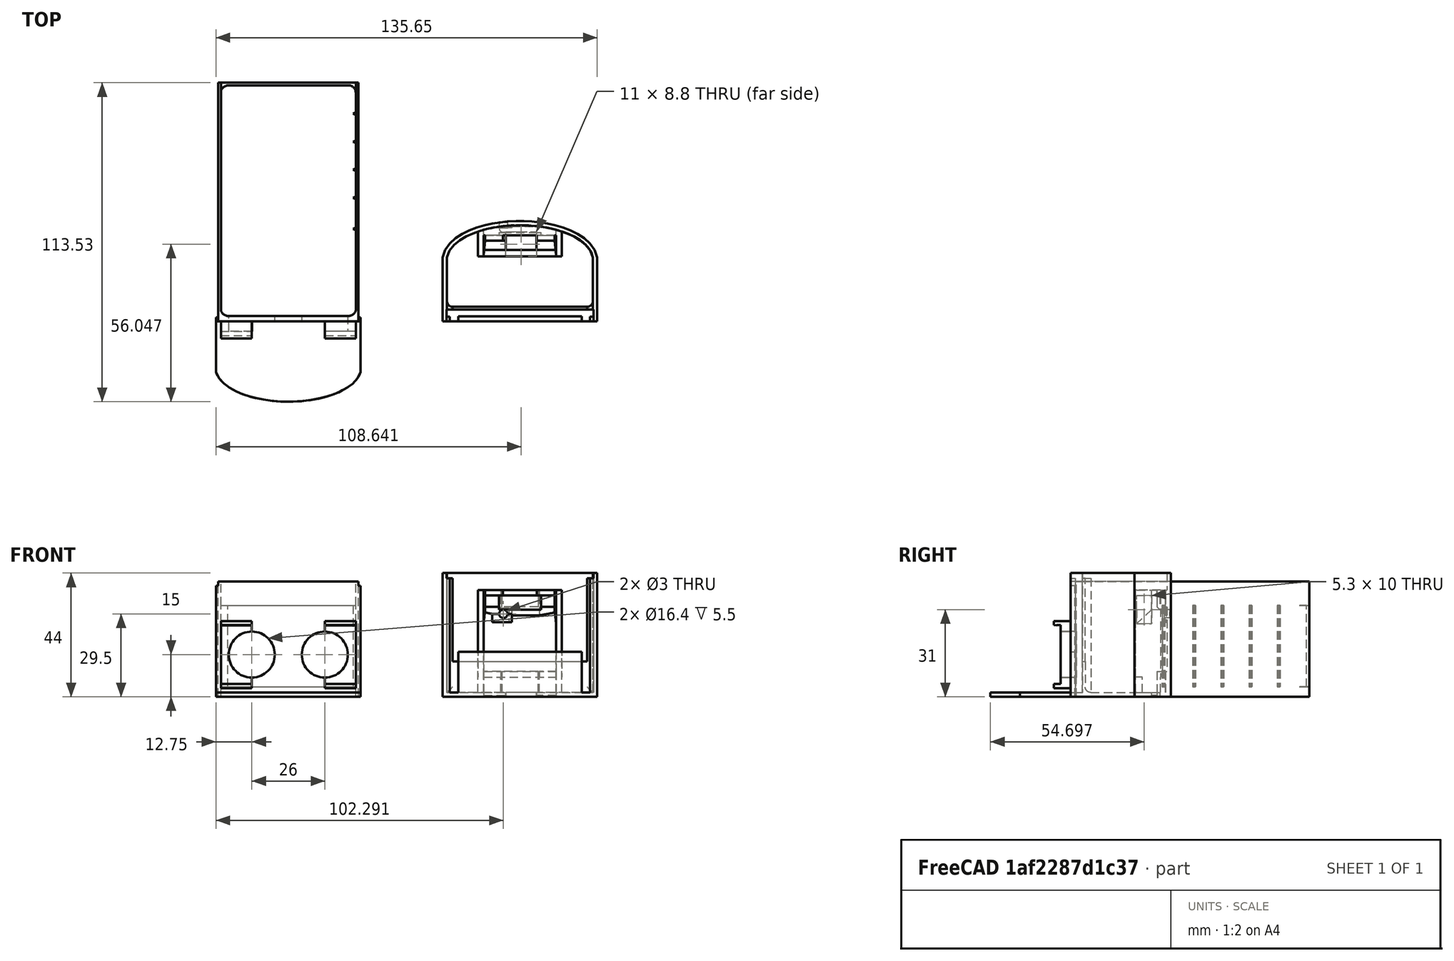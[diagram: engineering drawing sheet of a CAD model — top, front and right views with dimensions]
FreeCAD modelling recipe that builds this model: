
FCSTD DOCUMENT  (FreeCAD 0.18.4R)
Label: sonic.sensor.V6
License: All rights reserved
LicenseURL: http://en.wikipedia.org/wiki/All_rights_reserved
objects: Part::Feature×10, Part::Extrusion×10, Part::Cut×9, Part::Part2DObjectPython×5, Part::MultiFuse×2
note: 36 computed .brp shape members not serialized (recipe doc carries the construction recipe); baked Part::Feature solids carry a one-line shape summary decoded from their .brp

FEATURE [Part::Feature] Fusion025001001  label="Fusion025007"
  shape: bbox 51.5 x 91 x 41 mm, 79 faces (baked)
FEATURE [Part::Feature] Cut047001  label="Cut048"
  shape: bbox 54.92 x 35.75 x 44 mm, 100 faces (baked)
FEATURE [Part::Feature] Cut  label="Cut047008"
  Placement = pos=(-82.4397,-54.2833,45.5) rot=(1,0,0;3.14159rad)
  shape: bbox 51.9 x 28.53 x 1.5 mm, 8 faces (baked)
FEATURE [Part::Feature] Face001
  Placement = pos=(-82.4397,-54.2833,45.5) rot=(1,0,0;3.14159rad)
  shape: bbox 1.021e-05 x 15.53 x 1.5 mm, 1 faces, 0 solids (baked)
FEATURE [Part::Extrusion] Extrusion
  Base = -> Face001
  Dir = (-0.202449,-2e-16,0)
  DirMode = 0
  FaceMakerClass = Part::FaceMakerBullseye
  LengthFwd = 0
  LengthRev = 0
  Solid = true
  Symmetric = false
FEATURE [Part::Feature] Face002
  Placement = pos=(-82.4397,-54.2833,45.5) rot=(1,0,0;3.14159rad)
  shape: bbox 1.02e-05 x 1.5 x 1.5 mm, 1 faces, 0 solids (baked)
FEATURE [Part::Extrusion] Extrusion001
  Base = -> Face002
  Dir = (-0.2,0,0)
  DirMode = 0
  FaceMakerClass = Part::FaceMakerBullseye
  LengthFwd = 0
  LengthRev = 0
  Solid = true
  Symmetric = false
FEATURE [Part::Cut] Cut047002
  Base = -> Cut
  Tool = -> Extrusion001
FEATURE [Part::Cut] Cut047003
  Base = -> Cut047002
  Tool = -> Extrusion
FEATURE [Part::Feature] Face
  Placement = pos=(-82.4397,-54.2833,45.5) rot=(1,0,0;3.14159rad)
  shape: bbox 1.022e-05 x 17.03 x 1.5 mm, 1 faces, 0 solids (baked)
FEATURE [Part::Extrusion] Extrusion002
  Base = -> Face
  Dir = (0.2,3.56116e-11,0)
  DirMode = 0
  FaceMakerClass = Part::FaceMakerBullseye
  LengthFwd = 0
  LengthRev = 0
  Solid = true
  Symmetric = false
FEATURE [Part::Cut] Cut047004
  Base = -> Cut047003
  Tool = -> Extrusion002
FEATURE [Part::Part2DObjectPython] Rectangle  # Draft 2D object (typed FeaturePython)
  ChamferSize = 0
  Columns = 1
  FilletRadius = 0
  Height = 6.48539
  Length = 13.196
  MakeFace = true
  Placement = pos=(50.75,-56.2171,-3.37764) rot=(0.57735,0.57735,0.57735;2.0944rad)
  Rows = 1
  Support = -> [Cut047004]
FEATURE [Part::Extrusion] Extrusion003
  Base = -> Rectangle
  Dir = (5.57169,3.7e-15,-3.1e-15)
  DirMode = 0
  FaceMakerClass = Part::FaceMakerBullseye
  LengthFwd = 0
  LengthRev = 0
  Solid = true
  Symmetric = false
FEATURE [Part::Cut] Cut047005
  Base = -> Cut047004
  Tool = -> Extrusion003
FEATURE [Part::Part2DObjectPython] Rectangle001  # Draft 2D object (typed FeaturePython)
  ChamferSize = 0
  Columns = 1
  FilletRadius = 0
  Height = 9.74903
  Length = 15.1226
  MakeFace = true
  Placement = pos=(-0.75,-44.1427,-2.99245) rot=(0.57735,-0.57735,-0.57735;2.0944rad)
  Rows = 1
  Support = -> [Cut047005]
FEATURE [Part::Extrusion] Extrusion004
  Base = -> Rectangle001
  Dir = (-5.48636,-1.54403e-09,1.54403e-09)
  DirMode = 0
  FaceMakerClass = Part::FaceMakerBullseye
  LengthFwd = 0
  LengthRev = 0
  Solid = true
  Symmetric = false
FEATURE [Part::Cut] Cut047006
  Base = -> Cut047005
  Tool = -> Extrusion004
FEATURE [Part::MultiFuse] Fusion
  Shapes = -> [Cut047006,Fusion025001001]
FEATURE [Part::Part2DObjectPython] Rectangle002  # Draft 2D object (typed FeaturePython)
  ChamferSize = 0
  Columns = 1
  FilletRadius = 0
  Height = 15.8443
  Length = 3.14753
  MakeFace = true
  Placement = pos=(130.245,-38.6276,44) rot=(0,0,1;0rad)
  Rows = 1
FEATURE [Part::Part2DObjectPython] Rectangle004  # Draft 2D object (typed FeaturePython)
  ChamferSize = 0
  Columns = 1
  FilletRadius = 0
  Height = 15.3179
  Length = 4.9835
  MakeFace = true
  Placement = pos=(81.4897,-38.1013,44) rot=(0,0,1;0rad)
  Rows = 1
FEATURE [Part::Part2DObjectPython] Line001  # Draft 2D object (typed FeaturePython)
  ChamferSize = 0
  Closed = false
  End = (-0.75,-37.0713,5.991e-13)
  FilletRadius = 0
  Length = 1.5
  MakeFace = true
  Placement = pos=(-0.75,-37.0713,1.5) rot=(0.57735,-0.57735,-0.57735;2.0944rad)
  Points = (2) [(0,0,0),(-1.25084e-10,-1.5,-2.62753e-09)]
  Start = (-0.75,-37.0713,1.5)
  Subdivisions = 0
  Support = -> [Fusion]
FEATURE [Part::Extrusion] Extrusion005
  Base = -> Rectangle004
  Dir = (-1e-16,4e-16,-1.8)
  DirMode = 0
  FaceMakerClass = Part::FaceMakerBullseye
  LengthFwd = 0
  LengthRev = 0
  Solid = true
  Symmetric = false
FEATURE [Part::Extrusion] Extrusion006
  Base = -> Rectangle002
  Dir = (-1e-16,4e-16,-1.8)
  DirMode = 0
  FaceMakerClass = Part::FaceMakerBullseye
  LengthFwd = 0
  LengthRev = 0
  Solid = true
  Symmetric = false
FEATURE [Part::Cut] Cut047007
  Base = -> Cut047001
  Tool = -> Extrusion006
FEATURE [Part::Cut] Cut047008  label="Cut047009"
  Base = -> Cut047007
  Tool = -> Extrusion005
FEATURE [Part::Feature] Face003
  shape: bbox 1.02e-05 x 1.717 x 1.8 mm, 1 faces, 0 solids (baked)
FEATURE [Part::Extrusion] Extrusion007
  Base = -> Face003
  Dir = (-0.2,0,0)
  DirMode = 0
  FaceMakerClass = Part::FaceMakerBullseye
  LengthFwd = 0
  LengthRev = 0
  Solid = true
  Symmetric = false
FEATURE [Part::Cut] Cut047009  label="Cut047010"
  Base = -> Cut047008
  Tool = -> Extrusion007
FEATURE [Part::Feature] Face004
  shape: bbox 1.02e-05 x 1.717 x 1.8 mm, 1 faces, 0 solids (baked)
FEATURE [Part::Extrusion] Extrusion008
  Base = -> Face004
  Dir = (0.2,0,0)
  DirMode = 0
  FaceMakerClass = Part::FaceMakerBullseye
  LengthFwd = 0
  LengthRev = 0
  Solid = true
  Symmetric = false
FEATURE [Part::Cut] Cut047010  label="Cut047011"
  Base = -> Cut047009
  Tool = -> Extrusion008
FEATURE [Part::Feature] Face005
  shape: bbox 29.8 x 1.013e-05 x 36.5 mm, 1 faces, 0 solids (baked)
FEATURE [Part::Extrusion] Extrusion009
  Base = -> Face005
  Dir = (-1.47576e-11,-0.4,-9.4894e-12)
  DirMode = 0
  FaceMakerClass = Part::FaceMakerBullseye
  LengthFwd = 0
  LengthRev = 0
  Solid = true
  Symmetric = false
FEATURE [Part::MultiFuse] Fusion025001002
  Shapes = -> [Cut047010,Extrusion009]
FEATURE [Part::Feature] Fusion025001002001  label="Fusion025001003"
  shape: bbox 54.92 x 35.75 x 44 mm, 105 faces (baked)
